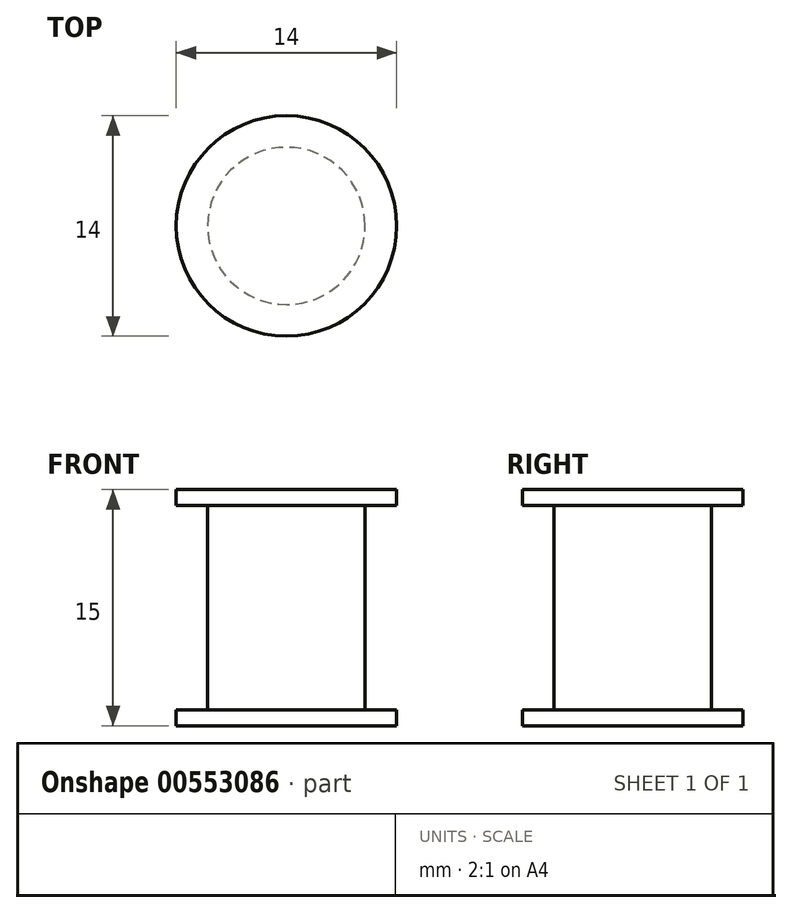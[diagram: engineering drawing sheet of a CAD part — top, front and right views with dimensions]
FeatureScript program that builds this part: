
annotation { "Feature Type Name" : "Feature", "Feature Type Description" : "" }
export const myFeature = defineFeature(function(context is Context, id is Id, definition is map)
    precondition{}
    {
        {
            var Q0;
            Q0=qCreatedBy(makeId("Top.planeOp"),FACE);
            var sketch = newSketch(context, id + "F0", { "sketchPlane" : qUnion([Q0])});
            skCircle(sketch, "E0", {"center": v(0, 0) * mm, "radius": 5 * mm});
            skSolve(sketch);
        }
        {
            var Q0;
            Q0=makeQuery(id+"F0.imprint","IMPRINT",FACE,{"disambiguationData":[TD([[makeQuery(id+"F0.imprint","IMPRINT",EDGE,{"derivedFrom":sQuery(id+"F0.wireOp",EDGE,"E0")}),1.0]])]});
            extrude(context, id + "F1", {"entities" : qUnion([Q0]), "depth" : 15 * mm, "offsetDistance" : 25 * mm});
        }
        {
            var Q0;
            Q0=qCreatedBy(makeId("Top.planeOp"),FACE);
            var sketch = newSketch(context, id + "F2", { "sketchPlane" : qUnion([Q0])});
            skCircle(sketch, "E1", {"center": v(0, 0) * mm, "radius": 7 * mm});
            skCircle(sketch, "E2", {"center": v(0, 0) * mm, "radius": 2.75 * mm});
            skSolve(sketch);
        }
        {
            var Q0;
            Q0=makeQuery(id+"F2.imprint","IMPRINT",FACE,{"disambiguationData":[TD([[makeQuery(id+"F2.imprint","IMPRINT",EDGE,{"derivedFrom":sQuery(id+"F2.wireOp",EDGE,"E1")}),1.0]])]});
            extrude(context, id + "F3", {"entities" : qUnion([Q0]), "operationType" : NewBodyOperationType.ADD, "depth" : 1 * mm, "offsetDistance" : 25 * mm});
        }
        {
            var Q0;
            Q0=makeQuery(id+"F1.opExtrude","CAP_FACE",FACE,{"disambiguationData":[OSD([sQuery(id+"F0.wireOp",EDGE,"E0")])],"isStart":false});
            var sketch = newSketch(context, id + "F4", { "sketchPlane" : qUnion([Q0])});
            skCircle(sketch, "E3", {"center": v(0, 0) * mm, "radius": 7 * mm});
            skSolve(sketch);
        }
        {
            var Q0;
            Q0 = qSketchRegion(id + "F4", true);
            extrude(context, id + "F5", {"entities" : qUnion([Q0]), "operationType" : NewBodyOperationType.ADD, "oppositeDirection" : true, "depth" : 1 * mm, "offsetDistance" : 25 * mm});
        }
    });
